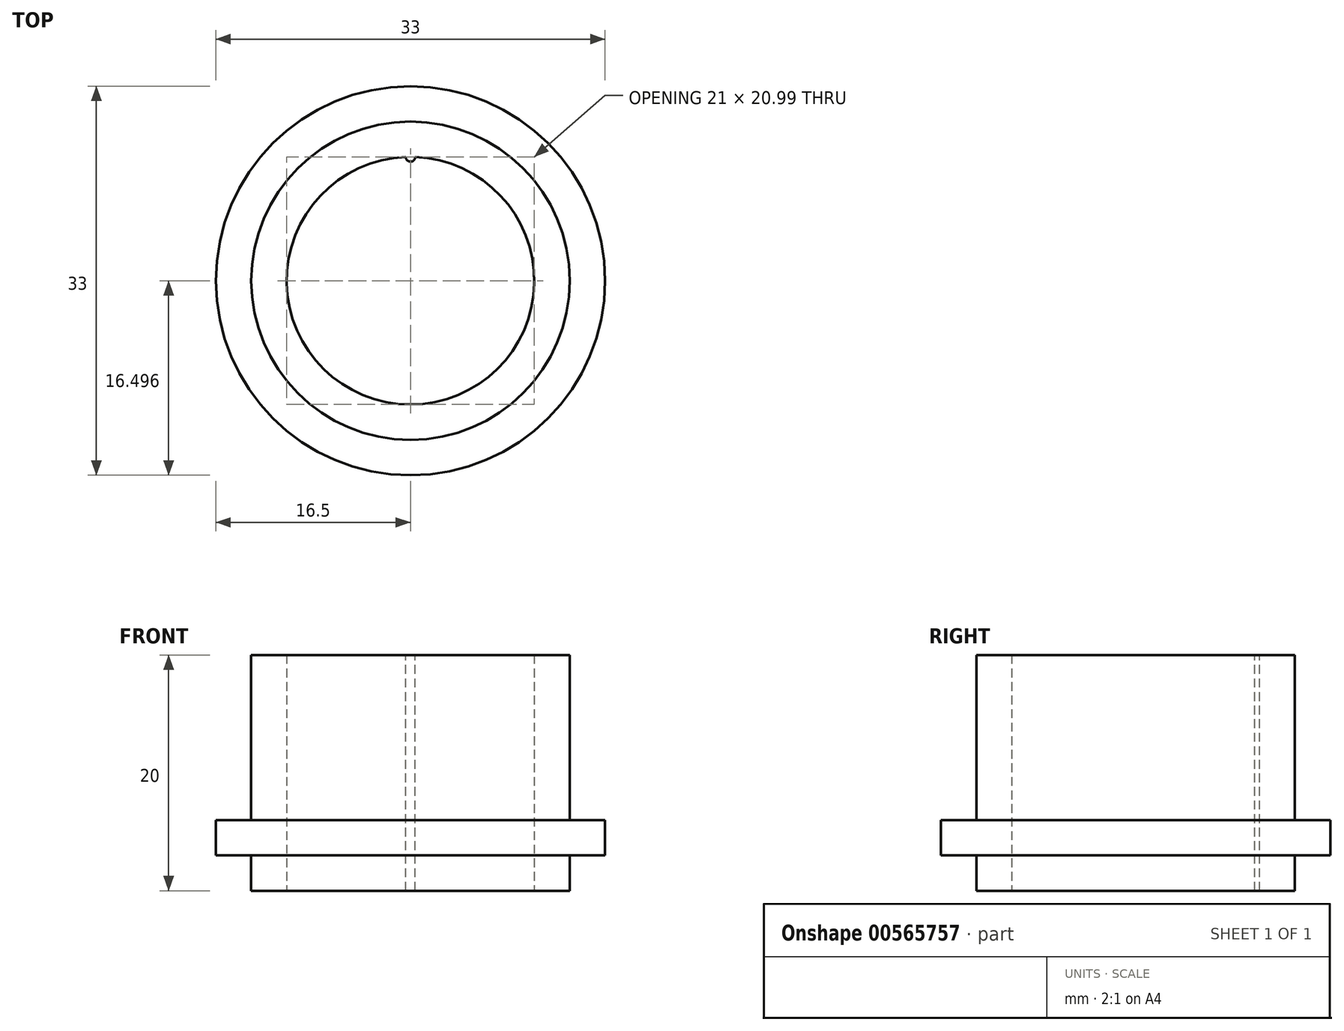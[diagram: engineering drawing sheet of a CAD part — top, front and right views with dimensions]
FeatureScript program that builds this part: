
annotation { "Feature Type Name" : "Feature", "Feature Type Description" : "" }
export const myFeature = defineFeature(function(context is Context, id is Id, definition is map)
    precondition{}
    {
        {
            var Q0;
            Q0=qCreatedBy(makeId("Front.planeOp"),FACE);
            var sketch = newSketch(context, id + "F0", { "sketchPlane" : qUnion([Q0])});
            skLineSegment(sketch, "E0", {"start": v(0, 1.48) * mm, "end": v(0, 57.6) * mm, "construction": true});
            skLineSegment(sketch, "E1", {"start": v(-10.5, -3) * mm, "end": v(-10.5, 17) * mm});
            skLineSegment(sketch, "E2", {"start": v(-10.5, 17) * mm, "end": v(-13.5, 17) * mm});
            skLineSegment(sketch, "E3", {"start": v(-13.5, 17) * mm, "end": v(-13.5, 3) * mm});
            skLineSegment(sketch, "E4", {"start": v(-13.5, 3) * mm, "end": v(-16.5, 3) * mm});
            skLineSegment(sketch, "E5", {"start": v(-16.5, 3) * mm, "end": v(-16.5, 0) * mm});
            skLineSegment(sketch, "E6", {"start": v(-16.5, 0) * mm, "end": v(-13.5, 0) * mm});
            skLineSegment(sketch, "E7", {"start": v(-13.5, 0) * mm, "end": v(-13.5, -3) * mm});
            skLineSegment(sketch, "E8", {"start": v(-13.5, -3) * mm, "end": v(-10.5, -3) * mm});
            skSolve(sketch);
        }
        {
            var Q0;
            Q0 = qSketchRegion(id + "F0", true);
            var Q1;
            Q1=sQuery(id+"F0.wireOp",EDGE,"E0");
            revolve(context, id + "F1", {"surfaceOperationType" : NewSurfaceOperationType.NEW, "entities" : qUnion([Q0]), "axis" : qUnion([Q1]), "revolveType" : RevolveType.FULL});
        }
        {
            var Q0;
            Q0=makeQuery(id+"F1.opRevolve","SWEPT_FACE",FACE,{"disambiguationData":[OSD([sQuery(id+"F0.wireOp",EDGE,"E2")])]});
            var sketch = newSketch(context, id + "F2", { "sketchPlane" : qUnion([Q0])});
            skArc(sketch, "E9", {"start": v(-0.4, 10.5) * mm, "mid": v(0, 10.1) * mm, "end": v(0.4, 10.5) * mm});
            skSolve(sketch);
        }
        {
            var Q0;
            {var subQ0=sQuery(id+"F2.wireOp",EDGE,"E9");Q0=makeQuery(id+"F2.imprint","IMPRINT",FACE,{"disambiguationData":[TD([[makeQuery(id+"F2.imprint","IMPRINT",EDGE,{"derivedFrom":subQ0}),1.0]])]});}
            var Q1;
            Q1=makeQuery(id+"F1.opRevolve","SWEPT_FACE",FACE,{"disambiguationData":[OSD([sQuery(id+"F0.wireOp",EDGE,"E8")])]});
            extrude(context, id + "F3", {"entities" : qUnion([Q0]), "operationType" : NewBodyOperationType.ADD, "endBound" : BoundingType.UP_TO_SURFACE, "oppositeDirection" : true, "depth" : 25 * mm, "endBoundEntityFace" : qUnion([Q1]), "offsetDistance" : 25 * mm});
        }
    });
